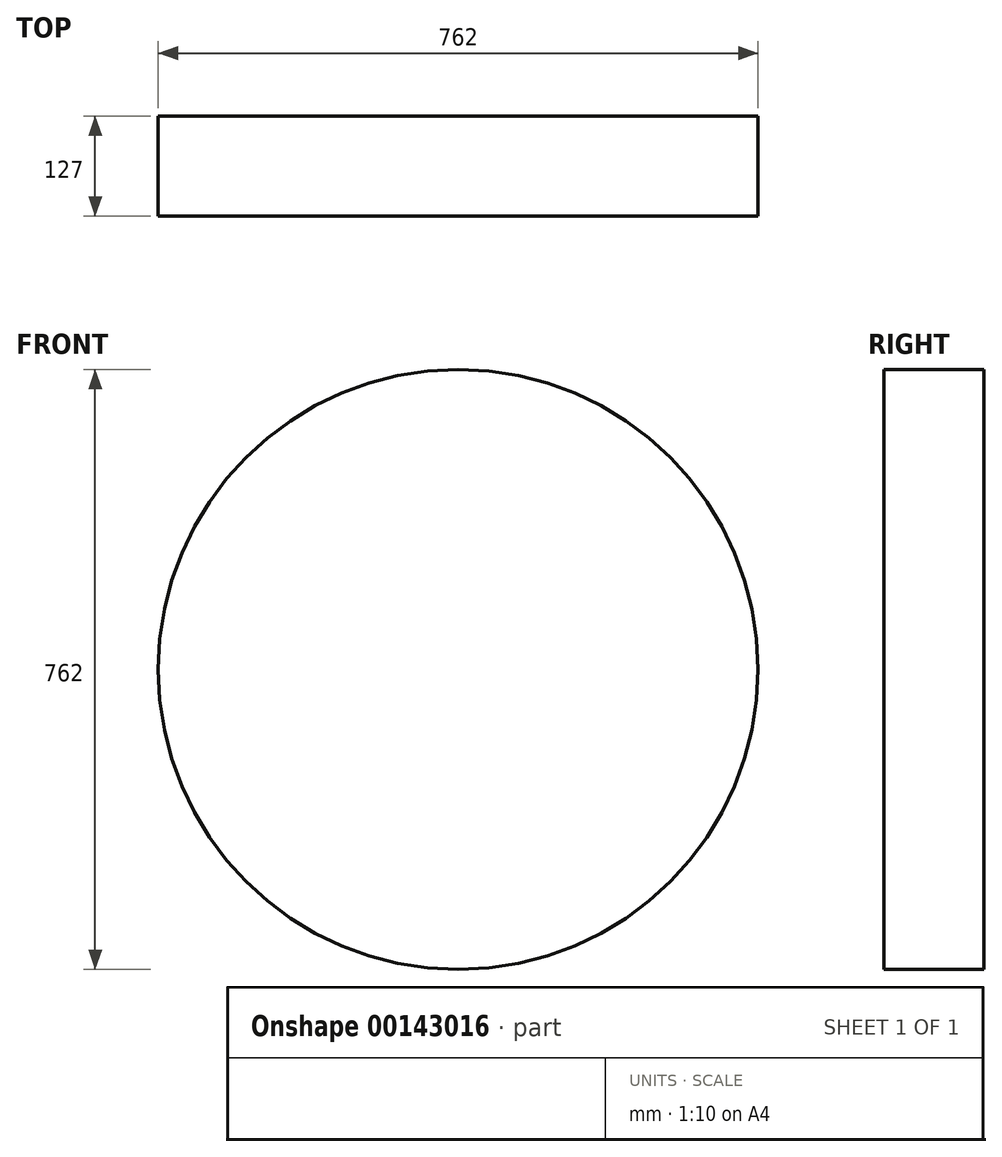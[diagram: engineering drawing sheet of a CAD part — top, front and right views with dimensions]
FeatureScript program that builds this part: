
annotation { "Feature Type Name" : "Feature", "Feature Type Description" : "" }
export const myFeature = defineFeature(function(context is Context, id is Id, definition is map)
    precondition{}
    {
        {
            var Q0;
            Q0=qCreatedBy(makeId("Front.planeOp"),FACE);
            var sketch = newSketch(context, id + "F0", { "sketchPlane" : qUnion([Q0])});
            skCircle(sketch, "E0", {"center": v(0, 0) * mm, "radius": 184.15 * mm});
            skSolve(sketch);
        }
        {
            var Q0;
            Q0=makeQuery(id+"F0.imprint","IMPRINT",FACE,{"disambiguationData":[TD([[makeQuery(id+"F0.imprint","IMPRINT",EDGE,{"derivedFrom":sQuery(id+"F0.wireOp",EDGE,"E0")}),1.0]])]});
            var sketch = newSketch(context, id + "F1", { "sketchPlane" : qUnion([Q0])});
            skCircle(sketch, "E1", {"center": v(0, 0) * mm, "radius": 381 * mm});
            skSolve(sketch);
        }
        {
            var Q0;
            Q0 = qSketchRegion(id + "F1", true);
            extrude(context, id + "F2", {"entities" : qUnion([Q0]), "oppositeDirection" : true, "depth" : 127 * mm});
        }
    });
